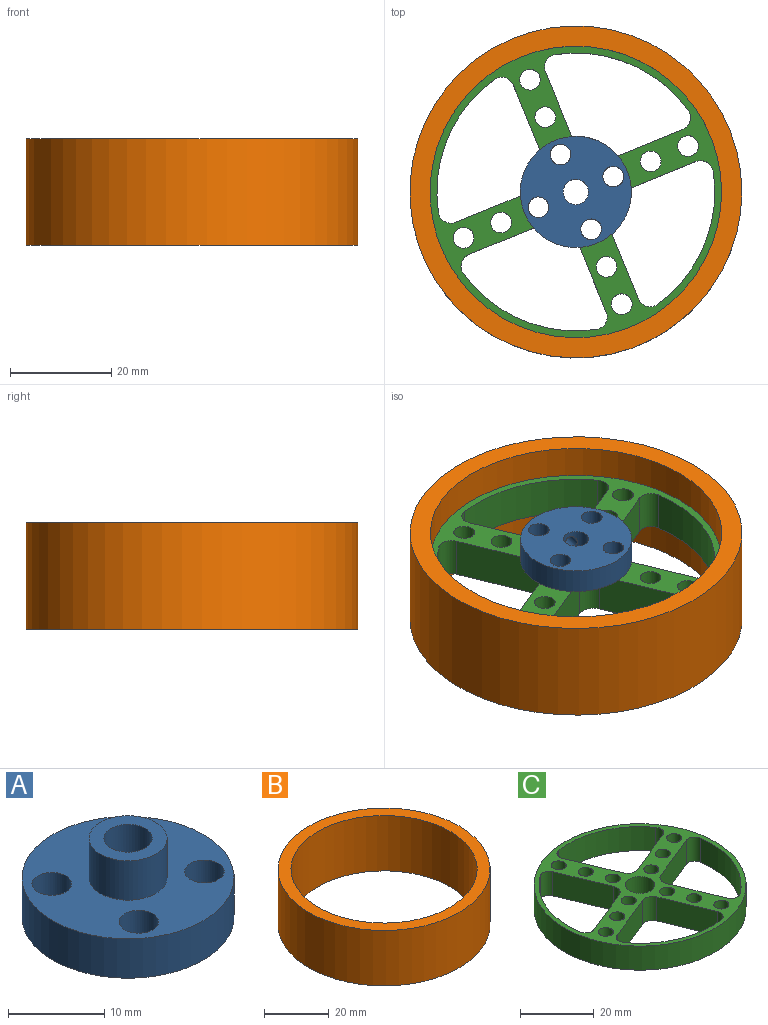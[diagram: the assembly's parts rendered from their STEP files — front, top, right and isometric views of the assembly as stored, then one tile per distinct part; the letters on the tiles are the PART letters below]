
ASSEMBLY  parts=3 mates=3
PART A: 11 faces, bbox 22x22x10 mm
  f0: cylinder r=2.05mm len=5mm, axis (0,0,-1), area 64.4mm2, adj f5,f6
  f1: cylinder r=2.05mm len=5mm, axis (0,0,-1), area 64.4mm2, adj f5,f6
  f2: cylinder r=2.05mm len=5mm, axis (0,0,-1), area 64.4mm2, adj f5,f6
  f3: cylinder r=2.05mm len=5mm, axis (0,0,-1), area 64.4mm2, adj f5,f6
  f4: cylinder r=11mm len=22mm, axis (0,0,-1), area 338.9mm2, adj f5,f6,f10
  f5: plane 22x22mm, normal (0,0,1), area 275.8mm2, adj f0,f1,f2,f3,f4,f8
  f6: plane 22x22mm, normal (0,0,-1), area 307.7mm2, adj f0,f1,f2,f3,f4,f7
  f7: cylinder r=2.5mm len=10mm, axis (0,0,-1), area 150.2mm2, adj f6,f9,f10
  f8: cylinder r=4.05mm len=8.1mm, axis (0,0,-1), area 127.2mm2, adj f5,f9
  f9: plane 8.1x8.1mm, normal (0,0,1), area 31.9mm2, adj f7,f8
  f10: cylinder r=1.45mm len=8.96mm, axis (0,-1,0), area 79.1mm2, adj f4,f7
PART B: 4 faces, bbox 65.7x65.7x21 mm
  f0: cylinder r=28.85mm len=57.7mm, axis (0,0,-1), area 3806.7mm2, adj f2,f3
  f1: cylinder r=32.85mm len=65.7mm, axis (0,0,-1), area 4334.5mm2, adj f2,f3
  f2: plane 65.7x65.7mm, normal (0,0,1), area 775.3mm2, adj f0,f1
  f3: plane 65.7x65.7mm, normal (0,0,-1), area 775.3mm2, adj f0,f1
PART C: 40 faces, bbox 57.7x57.7x8 mm
  f0: plane 16.52x8mm, normal (0.93,0.38,0), area 142.8mm2, adj f26,f27,f29,f36
  f1: cylinder r=27.5mm len=26.32mm, axis (0,0,-1), area 240.1mm2, adj f26,f27,f36,f37
  f2: cylinder r=27.5mm len=26.32mm, axis (0,0,-1), area 240.1mm2, adj f26,f27,f34,f35
  f3: plane 16.52x8mm, normal (-0.93,-0.38,0), area 142.8mm2, adj f26,f27,f28,f35
  f4: cylinder r=27.5mm len=26.32mm, axis (0,0,-1), area 240.1mm2, adj f26,f27,f32,f33
  f5: plane 16.52x8mm, normal (0.38,-0.93,0), area 142.8mm2, adj f26,f27,f30,f33
  f6: cylinder r=27.5mm len=26.32mm, axis (0,0,-1), area 240.1mm2, adj f26,f27,f38,f39
  f7: plane 16.52x8mm, normal (0.93,0.38,0), area 142.8mm2, adj f26,f27,f31,f39
  f8: cylinder r=2.05mm len=8mm, axis (0,0,-1), area 103mm2, adj f26,f27
  f9: cylinder r=2.05mm len=8mm, axis (0,0,-1), area 103mm2, adj f26,f27
  f10: cylinder r=2.05mm len=8mm, axis (0,0,-1), area 103mm2, adj f26,f27
  f11: cylinder r=2.05mm len=8mm, axis (0,0,-1), area 103mm2, adj f26,f27
  f12: cylinder r=2.05mm len=8mm, axis (0,0,-1), area 103mm2, adj f26,f27
  f13: cylinder r=2.05mm len=8mm, axis (0,0,-1), area 103mm2, adj f26,f27
  f14: cylinder r=2.05mm len=8mm, axis (0,0,-1), area 103mm2, adj f26,f27
  f15: cylinder r=2.05mm len=8mm, axis (0,0,-1), area 103mm2, adj f26,f27
  f16: cylinder r=2.05mm len=8mm, axis (0,0,-1), area 103mm2, adj f26,f27
  f17: cylinder r=2.05mm len=8mm, axis (0,0,-1), area 103mm2, adj f26,f27
  f18: cylinder r=2.05mm len=8mm, axis (0,0,-1), area 103mm2, adj f26,f27
  f19: cylinder r=4mm len=8mm, axis (0,0,-1), area 201.1mm2, adj f26,f27
  f20: cylinder r=28.85mm len=57.7mm, axis (0,0,-1), area 1450.2mm2, adj f26,f27
  f21: plane 16.52x8mm, normal (-0.38,0.93,0), area 142.8mm2, adj f26,f27,f29,f37
  f22: plane 16.52x8mm, normal (-0.38,0.93,0), area 142.8mm2, adj f26,f27,f28,f34
  f23: plane 16.52x8mm, normal (-0.93,-0.38,0), area 142.8mm2, adj f26,f27,f30,f32
  f24: plane 16.52x8mm, normal (0.38,-0.93,0), area 142.8mm2, adj f26,f27,f31,f38
  f25: cylinder r=2.05mm len=8mm, axis (0,0,-1), area 103mm2, adj f26,f27
  f26: plane 57.7x57.7mm, normal (0,0,1), area 761.4mm2, adj f0,f1,f2,f3,f4,f5,f6,f7
  f27: plane 57.7x57.7mm, normal (0,0,-1), area 761.4mm2, adj f0,f1,f2,f3,f4,f5,f6,f7
  f28: cylinder r=3mm len=8mm, axis (0,0,-1), area 37.7mm2, adj f3,f22,f26,f27
  f29: cylinder r=3mm len=8mm, axis (0,0,-1), area 37.7mm2, adj f0,f21,f26,f27
  f30: cylinder r=3mm len=8mm, axis (0,0,-1), area 37.7mm2, adj f5,f23,f26,f27
  f31: cylinder r=3mm len=8mm, axis (0,0,-1), area 37.7mm2, adj f7,f24,f26,f27
  f32: cylinder r=2.5mm len=8mm, axis (0,0,-1), area 36.2mm2, adj f4,f23,f26,f27
  f33: cylinder r=2.5mm len=8mm, axis (0,0,-1), area 36.2mm2, adj f4,f5,f26,f27
  f34: cylinder r=2.5mm len=8mm, axis (0,0,-1), area 36.2mm2, adj f2,f22,f26,f27
  f35: cylinder r=2.5mm len=8mm, axis (0,0,-1), area 36.2mm2, adj f2,f3,f26,f27
  f36: cylinder r=2.5mm len=8mm, axis (0,0,-1), area 36.2mm2, adj f0,f1,f26,f27
  f37: cylinder r=2.5mm len=8mm, axis (0,0,-1), area 36.2mm2, adj f1,f21,f26,f27
  f38: cylinder r=2.5mm len=8mm, axis (0,0,-1), area 36.2mm2, adj f6,f24,f26,f27
  f39: cylinder r=2.5mm len=8mm, axis (0,0,-1), area 36.2mm2, adj f6,f7,f26,f27
PLACE A rot(axis=(-0.13,-0.99,0),180deg) t=(-51.81,32.58,-17.75)mm
PLACE B t=(-51.81,32.58,-37.25)mm
PLACE C t=(-51.81,32.58,-30.75)mm fixed
MATE revolute A.f3 <-> C.f18  axis (0,0,-1) through (-54.83,39.99,-22.75)mm
MATE fastened C.f20 <-> B.f0  axis (0,0,-1) through (-51.81,32.58,-26.75)mm
MATE revolute A.f1 <-> C.f10  axis (0,0,-1) through (-48.78,25.18,-22.75)mm
